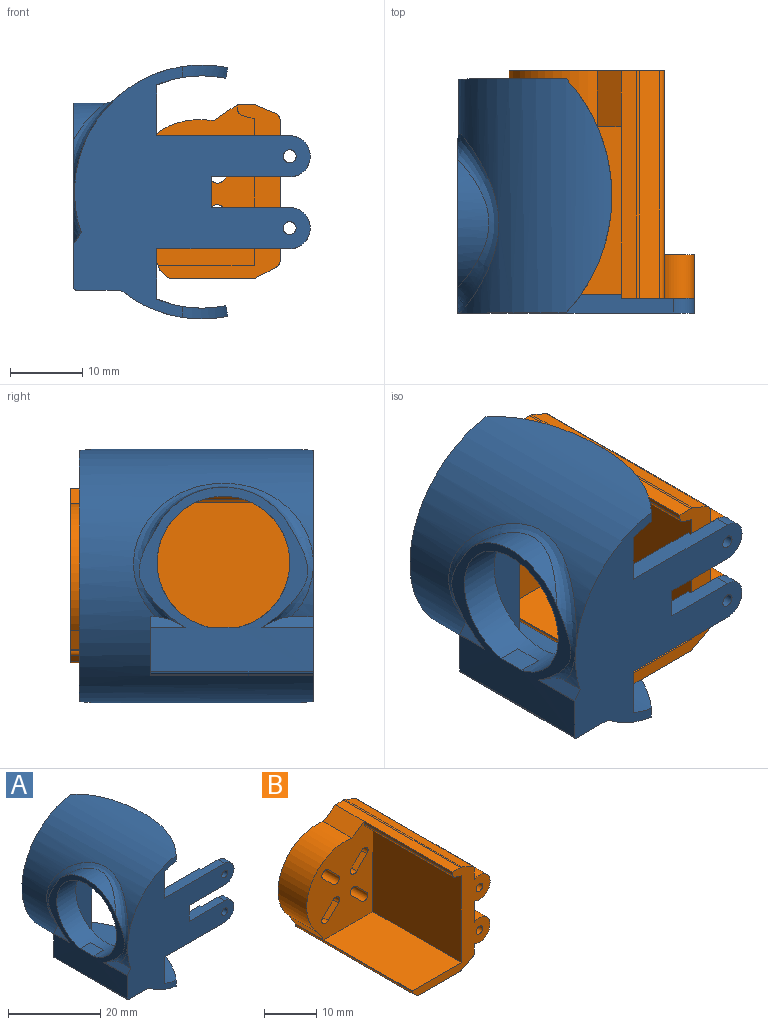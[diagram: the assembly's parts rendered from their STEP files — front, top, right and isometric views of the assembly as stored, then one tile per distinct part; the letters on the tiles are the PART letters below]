
ASSEMBLY  parts=2 mates=1
PART A: 57 faces, bbox 39.8x37.6x40.3 mm
  f0: plane 19.16x5.03mm, normal (0,0,-1), area 71.5mm2, adj f1,f2,f3,f51,f52,f54,f55,f56
  f1: cylinder r=16.09mm len=6.35mm, axis (0,1,0), area 20.6mm2, adj f0,f2,f56
  f2: cylinder r=10.45mm len=6.35mm, axis (-1,0,0), area 28.6mm2, adj f0,f1,f3,f56
  f3: plane 19.77x18.76mm, normal (1,0,0), area 59.2mm2, adj f0,f2,f4,f5,f46,f47,f48,f51
  f4: cylinder r=10.45mm len=5.58mm, axis (-1,0,0), area 12.2mm2, adj f3,f52,f56
  f5: cylinder r=9.19mm len=18.39mm, axis (-1,0,0), area 324.3mm2, adj f3,f6,f7,f8,f46
  f6: cylinder r=16.09mm len=4.03mm, axis (0,1,0), area 0.7mm2, adj f5,f7
  f7: plane 4.04x3.28mm, normal (0,0,1), area 13.2mm2, adj f5,f6,f8
  f8: plane 30.68x29.2mm, normal (-1,0,0), area 224.5mm2, adj f5,f7,f9,f38,f39,f40,f41,f42
  f9: plane 34.82x32.83mm, normal (0,-1,0), area 571.3mm2, adj f8,f10,f13,f16,f17,f18,f24,f25
  f10: cylinder r=0.9mm len=2.05mm, axis (0,-1,0), area 11.6mm2, adj f9,f11
  f11: plane 8x5.71mm, normal (0,1,0), area 39.7mm2, adj f10,f12,f25,f26,f27
  f12: plane 5.71x0.5mm, normal (1,0,0), area 2.9mm2, adj f11,f25,f27,f56
  f13: cylinder r=0.9mm len=2.05mm, axis (0,-1,0), area 11.6mm2, adj f9,f14
  f14: plane 8x5.71mm, normal (0,1,0), area 39.7mm2, adj f13,f15,f29,f30,f31
  f15: plane 5.71x0.5mm, normal (1,0,0), area 2.9mm2, adj f14,f29,f31,f56
  f16: plane 7.31x1.72mm, normal (-0.81,0,0.58), area 10.1mm2, adj f9,f17,f43,f44,f45
  f17: cylinder r=17.59mm len=6.58mm, axis (0,1,0), area 10.1mm2, adj f9,f16,f43
  f18: cylinder r=23.97mm len=16.2mm, axis (0,0,1), area 24mm2, adj f9,f19,f34,f52
  f19: plane 8.42x2.19mm, normal (0.98,0,-0.21), area 7.7mm2, adj f18,f20,f34,f52
  f20: cylinder r=23.97mm len=16.2mm, axis (0,0,1), area 24mm2, adj f19,f21,f34,f52
  f21: plane 34.77x14.92mm, normal (0,1,0), area 71.3mm2, adj f20,f22,f34,f52
  f22: cylinder r=23.97mm len=16.2mm, axis (0,0,1), area 24mm2, adj f21,f23,f34,f52
  f23: plane 8.42x2.19mm, normal (0.98,0,0.21), area 7.7mm2, adj f22,f33,f34,f52
  f24: plane 7.05x2.55mm, normal (1,0,0), area 18mm2, adj f9,f25,f52,f56
  f25: plane 18.42x2.55mm, normal (0,0,1), area 44.3mm2, adj f9,f11,f12,f24,f26,f56
  f26: cylinder r=2.86mm len=5.71mm, axis (0,-1,0), area 18.4mm2, adj f9,f11,f25,f27
  f27: plane 10.87x2.55mm, normal (0,0,-1), area 25.1mm2, adj f9,f11,f12,f26,f28,f56
  f28: plane 4.24x2.55mm, normal (1,0,0), area 10.8mm2, adj f9,f27,f29,f56
  f29: plane 10.87x2.55mm, normal (0,0,1), area 25.1mm2, adj f9,f14,f15,f28,f30,f56
  f30: cylinder r=2.86mm len=5.71mm, axis (0,-1,0), area 18.4mm2, adj f9,f14,f29,f31
  f31: plane 18.42x2.55mm, normal (0,0,-1), area 44.4mm2, adj f9,f14,f15,f30,f32,f56
  f32: plane 6.98x2.55mm, normal (1,0,0), area 17.8mm2, adj f9,f31,f52,f56
  f33: cylinder r=23.97mm len=16.2mm, axis (0,0,1), area 24mm2, adj f9,f23,f34,f52
  f34: cylinder r=17.59mm len=35.18mm, axis (0,1,0), area 1253.5mm2, adj f9,f18,f19,f20,f21,f22,f23,f33
  f35: plane 4.94x1.7mm, normal (-0.81,0,0.58), area 5.9mm2, adj f34,f39,f40,f41,f43
  f36: plane 22.51x0.69mm, normal (-0.33,0,-0.94), area 16.3mm2, adj f9,f34,f37,f39
  f37: plane 22.51x5.84mm, normal (0,0,-1), area 131.5mm2, adj f9,f36,f38,f39
  f38: cylinder r=0.3mm len=22.51mm, axis (0,1,0), area 10.6mm2, adj f8,f9,f37,f39
  f39: plane 8.17x6.83mm, normal (0,1,0), area 25mm2, adj f8,f34,f35,f36,f37,f38,f40
  f40: cylinder r=0.3mm len=4.8mm, axis (0,1,0), area 0.3mm2, adj f8,f35,f39
  f41: cylinder r=10.45mm len=0.6mm, axis (-1,0,0), area 0mm2, adj f8,f35,f43
  f42: cylinder r=10.45mm len=17.82mm, axis (-1,0,0), area 0mm2, adj f8,f43
  f43: bspline ~24.92x21.39mm, area 93.1mm2, adj f8,f9,f16,f17,f34,f35,f41,f42
  f44: cylinder r=10.45mm len=0.6mm, axis (-1,0,0), area 0mm2, adj f8,f16,f43
  f45: cylinder r=0.3mm len=7.15mm, axis (0,1,0), area 0.4mm2, adj f8,f9,f16
  f46: bspline ~4.66x0.39mm, area 0.5mm2, adj f3,f5,f52
  f47: cylinder r=10.45mm len=5.6mm, axis (-1,0,0), area 12.3mm2, adj f3,f48,f52
  f48: plane 29.69x9.81mm, normal (0,-1,0), area 185.1mm2, adj f3,f47,f49,f51,f52
  f49: plane 29.69x2mm, normal (1,0,0), area 59.4mm2, adj f48,f50,f52
  f50: plane 29.69x9.89mm, normal (0,1,0), area 212.1mm2, adj f49,f52
  f51: cylinder r=10.45mm len=6.37mm, axis (-1,0,0), area 28.7mm2, adj f0,f3,f48,f52
  f52: cylinder r=16.09mm len=32.43mm, axis (0,1,0), area 1098.6mm2, adj f0,f3,f4,f9,f18,f19,f20,f21
  f53: plane 19.16x7.14mm, normal (0,0,1), area 136.7mm2, adj f52,f54,f55,f56
  f54: plane 7.14x4.87mm, normal (0,-1,0), area 23mm2, adj f0,f52,f53,f55
  f55: plane 19.16x4.87mm, normal (1,0,0), area 93.2mm2, adj f0,f53,f54,f56
  f56: plane 29.69x23.98mm, normal (0,1,0), area 391.5mm2, adj f0,f1,f2,f3,f4,f12,f15,f24
PART B: 46 faces, bbox 25.7x31.5x24.2 mm
  f0: plane 23.78x0.54mm, normal (-1,0,0), area 12.9mm2, adj f2,f5,f12,f45
  f1: plane 23.78x1.61mm, normal (-0.26,0,-0.96), area 39.7mm2, adj f2,f6,f12,f45
  f2: cylinder r=1mm len=23.78mm, axis (0,1,0), area 31mm2, adj f0,f1,f12,f45
  f3: plane 31.53x19.51mm, normal (1,0,0), area 554.5mm2, adj f12,f13,f15,f16,f18,f19,f39,f44
  f4: plane 31.53x2.78mm, normal (0.39,0,0.92), area 95.2mm2, adj f12,f13,f39,f40
  f5: plane 31.53x2.13mm, normal (-0.02,0,1), area 67.3mm2, adj f0,f12,f13,f34,f40
  f6: plane 23.78x20.29mm, normal (-1,0,0), area 482.6mm2, adj f1,f7,f12,f45
  f7: plane 23.78x13.25mm, normal (0,0,1), area 315mm2, adj f6,f8,f12,f45
  f8: plane 31.53x0.12mm, normal (-1,0,0), area 3.9mm2, adj f7,f12,f13,f32,f41
  f9: plane 31.53x0.91mm, normal (-0.64,0,-0.76), area 37.4mm2, adj f12,f13,f41,f42
  f10: plane 31.53x11.09mm, normal (0,0,-1), area 349.8mm2, adj f12,f13,f42,f43
  f11: plane 31.53x2.84mm, normal (0.47,0,-0.89), area 101mm2, adj f12,f13,f43,f44
  f12: plane 24.17x21.03mm, normal (0,-1,0), area 143.4mm2, adj f0,f1,f2,f3,f4,f5,f6,f7
  f13: plane 24.17x21.46mm, normal (0,1,0), area 390.1mm2, adj f3,f4,f5,f8,f9,f10,f11,f20
  f14: cylinder r=0.9mm len=6mm, axis (0,-1,0), area 33.9mm2, adj f12,f16
  f15: cylinder r=2.86mm len=6mm, axis (0,-1,0), area 70.5mm2, adj f3,f12,f16
  f16: plane 5.71x4.19mm, normal (0,1,0), area 17.6mm2, adj f3,f14,f15
  f17: cylinder r=0.9mm len=6mm, axis (0,-1,0), area 33.9mm2, adj f12,f19
  f18: cylinder r=2.86mm len=6mm, axis (0,-1,0), area 70.5mm2, adj f3,f12,f19
  f19: plane 5.71x4.19mm, normal (0,1,0), area 17.6mm2, adj f3,f17,f18
  f20: plane 7.75x2.74mm, normal (0.71,0,0.7), area 29.9mm2, adj f13,f21,f38,f45
  f21: cylinder r=1mm len=7.75mm, axis (0,1,0), area 24.3mm2, adj f13,f20,f22,f45
  f22: plane 7.75x2.74mm, normal (-0.71,0,-0.7), area 29.9mm2, adj f13,f21,f38,f45
  f23: plane 7.75x2.74mm, normal (-0.7,0,0.71), area 29.9mm2, adj f13,f24,f35,f45
  f24: cylinder r=1mm len=7.75mm, axis (0,1,0), area 24.3mm2, adj f13,f23,f25,f45
  f25: plane 7.75x2.74mm, normal (0.7,0,-0.71), area 29.9mm2, adj f13,f24,f35,f45
  f26: plane 7.75x2.74mm, normal (-0.71,0,-0.7), area 29.9mm2, adj f13,f27,f36,f45
  f27: cylinder r=1mm len=7.75mm, axis (0,1,0), area 24.3mm2, adj f13,f26,f28,f45
  f28: plane 7.75x2.74mm, normal (0.71,0,0.7), area 29.9mm2, adj f13,f27,f36,f45
  f29: plane 7.75x2.74mm, normal (0.7,0,-0.71), area 29.9mm2, adj f13,f30,f37,f45
  f30: cylinder r=1mm len=7.75mm, axis (0,1,0), area 24.3mm2, adj f13,f29,f31,f45
  f31: plane 7.75x2.74mm, normal (-0.7,0,0.71), area 29.9mm2, adj f13,f30,f37,f45
  f32: plane 7.75x2.6mm, normal (-0.85,0,-0.53), area 23.7mm2, adj f8,f13,f33,f45
  f33: cylinder r=10.3mm len=17.59mm, axis (0,1,0), area 203mm2, adj f13,f32,f34,f45
  f34: plane 7.75x3.32mm, normal (-0.56,0,0.83), area 31mm2, adj f5,f13,f33,f45
  f35: cylinder r=1mm len=7.75mm, axis (0,1,0), area 24.3mm2, adj f13,f23,f25,f45
  f36: cylinder r=1mm len=7.75mm, axis (0,1,0), area 24.3mm2, adj f13,f26,f28,f45
  f37: cylinder r=1mm len=7.75mm, axis (0,1,0), area 24.3mm2, adj f13,f29,f31,f45
  f38: cylinder r=1mm len=7.75mm, axis (0,1,0), area 24.3mm2, adj f13,f20,f22,f45
  f39: cylinder r=1mm len=31.53mm, axis (0,-1,0), area 37mm2, adj f3,f4,f12,f13
  f40: cylinder r=1mm len=31.53mm, axis (0,1,0), area 13.2mm2, adj f4,f5,f12,f13
  f41: cylinder r=1mm len=31.53mm, axis (0,-1,0), area 27.4mm2, adj f8,f9,f12,f13
  f42: cylinder r=1mm len=31.53mm, axis (0,-1,0), area 22.1mm2, adj f9,f10,f12,f13
  f43: cylinder r=1mm len=31.53mm, axis (0,1,0), area 15.3mm2, adj f10,f11,f12,f13
  f44: cylinder r=1mm len=31.53mm, axis (0,-1,0), area 34.3mm2, adj f3,f11,f12,f13
  f45: plane 22.24x17.87mm, normal (0,-1,0), area 281.9mm2, adj f0,f1,f2,f6,f7,f20,f21,f22
PLACE A t=(15.89,-22.78,7.55)mm fixed
PLACE B t=(19.46,-5.4,7.64)mm
MATE fastened A.f13 <-> B.f17  axis (0,-1,0) through (-35.09,-36.93,2.55)mm
